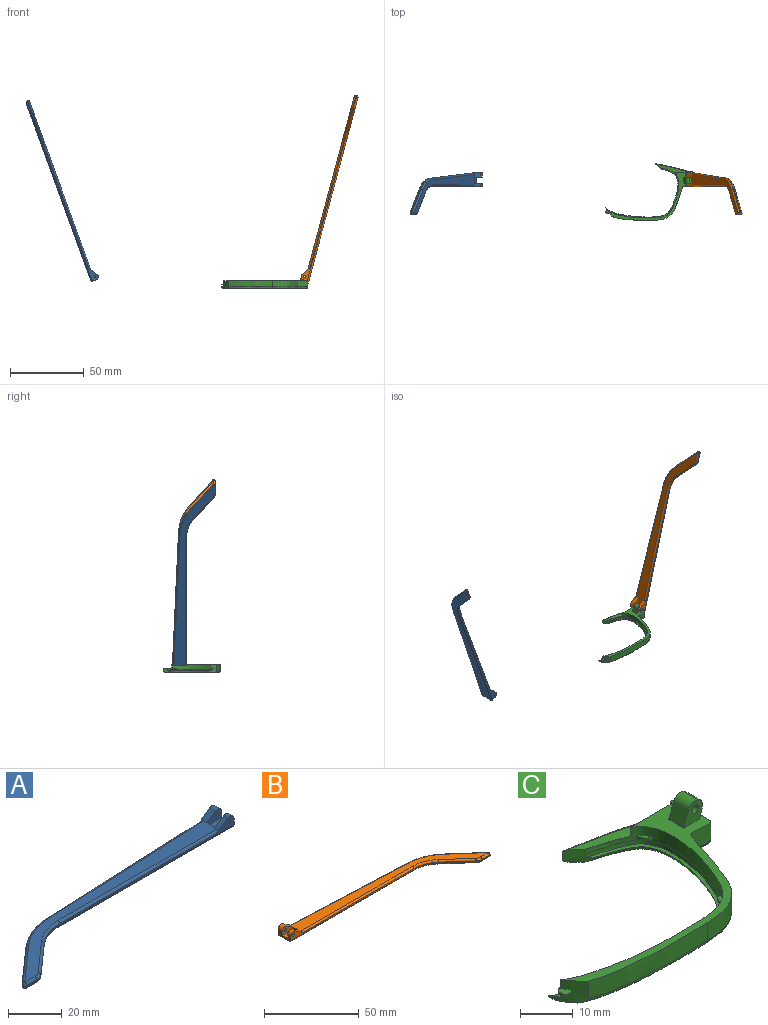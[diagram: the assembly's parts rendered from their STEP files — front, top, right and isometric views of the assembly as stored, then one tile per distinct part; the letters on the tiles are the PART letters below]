
ASSEMBLY  parts=3 mates=1
PART A: 43 faces, bbox 130.2x29.5x5.9 mm
  f0: plane 9.62x3.72mm, normal (1,0,0), area 24.7mm2, adj f1,f3,f4,f5,f10,f16,f18,f28
  f1: cylinder r=2.2mm len=3.45mm, axis (0,-1,0), area 11mm2, adj f0,f2,f4,f37
  f2: plane 6.01x3.91mm, normal (-0.55,0,0.84), area 12.7mm2, adj f1,f4,f9,f19,f37
  f3: plane 2.26x0.1mm, normal (0,0,1), area 0.1mm2, adj f0,f5,f18
  f4: plane 92.1x4.9mm, normal (0,-1,0), area 79.9mm2, adj f0,f1,f2,f14,f19,f36,f42
  f5: plane 93.42x4.13mm, normal (-0.04,1,0), area 64.8mm2, adj f0,f3,f11,f15,f17,f27,f28
  f6: plane 17.82x15.72mm, normal (-0.66,0.75,0), area 14.3mm2, adj f11,f12,f25,f30
  f7: plane 5.46x0.6mm, normal (0,-1,0), area 3.3mm2, adj f12,f13,f23,f32
  f8: plane 14.99x13.23mm, normal (0.66,-0.75,0), area 12mm2, adj f13,f14,f21,f34
  f9: plane 121.18x26.73mm, normal (0,0,1), area 627.7mm2, adj f2,f17,f19,f20,f21,f22,f23,f25
  f10: plane 129.1x27.08mm, normal (0,0,-1), area 686.5mm2, adj f0,f28,f29,f30,f32,f33,f34,f35
  f11: cylinder r=30mm len=18.52mm, axis (0,0,-1), area 12.2mm2, adj f5,f6,f26,f29
  f12: cylinder r=1mm len=1.75mm, axis (0,0,-1), area 1.5mm2, adj f6,f7,f24,f31
  f13: cylinder r=5mm len=3.31mm, axis (0,0,-1), area 2.2mm2, adj f7,f8,f22,f33
  f14: cylinder r=20mm len=13.23mm, axis (0,0,1), area 8.7mm2, adj f4,f8,f20,f35
  f15: plane 5.66x0.25mm, normal (0,0,-1), area 0.7mm2, adj f5,f17,f18
  f16: cylinder r=2.2mm len=3.45mm, axis (0,-1,0), area 14.8mm2, adj f0,f17,f18,f38
  f17: plane 6.01x3.91mm, normal (-0.55,0,0.84), area 16.9mm2, adj f5,f9,f15,f16,f18,f27,f38
  f18: plane 7.92x3.3mm, normal (0,1,0), area 15.9mm2, adj f0,f3,f15,f16,f17,f41
  f19: cylinder r=1mm len=84.18mm, axis (-1,0,0), area 131.4mm2, adj f2,f4,f9,f20
  f20: torus R=21mm, axis (0,0,1), area 23.1mm2, adj f9,f14,f19,f21
  f21: cylinder r=1mm len=15.65mm, axis (-0.75,-0.66,0), area 31.4mm2, adj f8,f9,f20,f22
  f22: torus R=4mm, axis (0,0,1), area 5.3mm2, adj f9,f13,f21,f23
  f23: cylinder r=1mm len=5.46mm, axis (-1,0,0), area 8.6mm2, adj f7,f9,f22,f24
  f24: sphere r=1mm, area 2.4mm2, adj f12,f23,f25
  f25: cylinder r=1mm len=18.48mm, axis (0.75,0.66,0), area 37.3mm2, adj f6,f9,f24,f26
  f26: torus R=29mm, axis (0,0,1), area 31.6mm2, adj f9,f11,f25,f27
  f27: cylinder r=1mm len=85.5mm, axis (1,0.04,0), area 133.5mm2, adj f5,f9,f17,f26
  f28: cylinder r=1mm len=93.46mm, axis (-1,-0.04,0), area 146.9mm2, adj f0,f5,f10,f29
  f29: torus R=29mm, axis (0,0,1), area 31.6mm2, adj f10,f11,f28,f30
  f30: cylinder r=1mm len=18.48mm, axis (-0.75,-0.66,0), area 37.3mm2, adj f6,f10,f29,f31
  f31: sphere r=1mm, area 2.4mm2, adj f12,f30,f32
  f32: cylinder r=1mm len=5.46mm, axis (1,0,0), area 8.6mm2, adj f7,f10,f31,f33
  f33: torus R=4mm, axis (0,0,1), area 5.3mm2, adj f10,f13,f32,f34
  f34: cylinder r=1mm len=15.65mm, axis (0.75,0.66,0), area 31.4mm2, adj f8,f10,f33,f35
  f35: torus R=21mm, axis (0,0,1), area 23.1mm2, adj f10,f14,f34,f36
  f36: cylinder r=1mm len=92.1mm, axis (1,0,0), area 144.7mm2, adj f0,f4,f10,f35
  f37: plane 7.92x4.7mm, normal (0,1,0), area 27mm2, adj f0,f1,f2,f39,f40,f42
  f38: plane 7.92x4.7mm, normal (0,-1,0), area 27mm2, adj f0,f16,f17,f39,f40,f41
  f39: plane 7.92x4.1mm, normal (0,0,1), area 32.5mm2, adj f0,f37,f38,f40
  f40: plane 4.1x1.4mm, normal (1,0,0), area 5.7mm2, adj f9,f37,f38,f39
  f41: cylinder r=0.5mm len=3.1mm, axis (0,-1,0), area 9.7mm2, adj f18,f38
  f42: cylinder r=0.5mm len=2.3mm, axis (0,-1,0), area 7.2mm2, adj f4,f37
PART B: 43 faces, bbox 130.2x29.5x5.9 mm
  f0: plane 9.62x3.72mm, normal (-1,0,0), area 24.7mm2, adj f1,f3,f4,f5,f10,f16,f18,f28
  f1: cylinder r=2.2mm len=3.45mm, axis (0,-1,0), area 11mm2, adj f0,f2,f4,f37
  f2: plane 6.01x3.91mm, normal (0.55,0,0.84), area 12.7mm2, adj f1,f4,f9,f19,f37
  f3: plane 2.26x0.1mm, normal (0,0,1), area 0.1mm2, adj f0,f5,f18
  f4: plane 92.1x4.9mm, normal (0,-1,0), area 78.2mm2, adj f0,f1,f2,f14,f19,f36,f42
  f5: plane 93.42x4.13mm, normal (0.04,1,0), area 64.8mm2, adj f0,f3,f11,f15,f17,f27,f28
  f6: plane 17.82x15.72mm, normal (0.66,0.75,0), area 14.3mm2, adj f11,f12,f25,f30
  f7: plane 5.46x0.6mm, normal (0,-1,0), area 3.3mm2, adj f12,f13,f23,f32
  f8: plane 14.99x13.23mm, normal (-0.66,-0.75,0), area 12mm2, adj f13,f14,f21,f34
  f9: plane 121.18x26.73mm, normal (0,0,1), area 627.7mm2, adj f2,f17,f19,f20,f21,f22,f23,f25
  f10: plane 129.1x27.08mm, normal (0,0,-1), area 686.5mm2, adj f0,f28,f29,f30,f32,f33,f34,f35
  f11: cylinder r=30mm len=18.52mm, axis (0,0,-1), area 12.2mm2, adj f5,f6,f26,f29
  f12: cylinder r=1mm len=1.75mm, axis (0,0,-1), area 1.5mm2, adj f6,f7,f24,f31
  f13: cylinder r=5mm len=3.31mm, axis (0,0,-1), area 2.2mm2, adj f7,f8,f22,f33
  f14: cylinder r=20mm len=13.23mm, axis (0,0,1), area 8.7mm2, adj f4,f8,f20,f35
  f15: plane 5.66x0.25mm, normal (0,0,-1), area 0.7mm2, adj f5,f17,f18
  f16: cylinder r=2.2mm len=3.45mm, axis (0,-1,0), area 14.8mm2, adj f0,f17,f18,f38
  f17: plane 6.01x3.91mm, normal (0.55,0,0.84), area 16.9mm2, adj f5,f9,f15,f16,f18,f27,f38
  f18: plane 7.92x3.3mm, normal (0,1,0), area 14.3mm2, adj f0,f3,f15,f16,f17,f41
  f19: cylinder r=1mm len=84.18mm, axis (1,0,0), area 131.4mm2, adj f2,f4,f9,f20
  f20: torus R=21mm, axis (0,0,1), area 23.1mm2, adj f9,f14,f19,f21
  f21: cylinder r=1mm len=15.65mm, axis (0.75,-0.66,0), area 31.4mm2, adj f8,f9,f20,f22
  f22: torus R=4mm, axis (0,0,1), area 5.3mm2, adj f9,f13,f21,f23
  f23: cylinder r=1mm len=5.46mm, axis (1,0,0), area 8.6mm2, adj f7,f9,f22,f24
  f24: sphere r=1mm, area 2.4mm2, adj f12,f23,f25
  f25: cylinder r=1mm len=18.48mm, axis (-0.75,0.66,0), area 37.3mm2, adj f6,f9,f24,f26
  f26: torus R=29mm, axis (0,0,1), area 31.6mm2, adj f9,f11,f25,f27
  f27: cylinder r=1mm len=85.5mm, axis (-1,0.04,0), area 133.5mm2, adj f5,f9,f17,f26
  f28: cylinder r=1mm len=93.46mm, axis (1,-0.04,0), area 146.9mm2, adj f0,f5,f10,f29
  f29: torus R=29mm, axis (0,0,1), area 31.6mm2, adj f10,f11,f28,f30
  f30: cylinder r=1mm len=18.48mm, axis (0.75,-0.66,0), area 37.3mm2, adj f6,f10,f29,f31
  f31: sphere r=1mm, area 2.4mm2, adj f12,f30,f32
  f32: cylinder r=1mm len=5.46mm, axis (-1,0,0), area 8.6mm2, adj f7,f10,f31,f33
  f33: torus R=4mm, axis (0,0,1), area 5.3mm2, adj f10,f13,f32,f34
  f34: cylinder r=1mm len=15.65mm, axis (-0.75,0.66,0), area 31.4mm2, adj f8,f10,f33,f35
  f35: torus R=21mm, axis (0,0,1), area 23.1mm2, adj f10,f14,f34,f36
  f36: cylinder r=1mm len=92.1mm, axis (-1,0,0), area 144.7mm2, adj f0,f4,f10,f35
  f37: plane 7.92x4.7mm, normal (0,1,0), area 25.4mm2, adj f0,f1,f2,f39,f40,f42
  f38: plane 7.92x4.7mm, normal (0,-1,0), area 25.4mm2, adj f0,f16,f17,f39,f40,f41
  f39: plane 7.92x4.1mm, normal (0,0,1), area 32.5mm2, adj f0,f37,f38,f40
  f40: plane 4.1x1.4mm, normal (-1,0,0), area 5.7mm2, adj f9,f37,f38,f39
  f41: cylinder r=0.88mm len=3.1mm, axis (0,-1,0), area 17mm2, adj f18,f38
  f42: cylinder r=0.88mm len=2.3mm, axis (0,-1,0), area 12.6mm2, adj f4,f37
PART C: 47 faces, bbox 79.8x39.4x10 mm
  f0: plane 0.12x0.12mm, normal (0,0,1), area 0mm2, adj f32,f43
  f1: plane 2.1x0.76mm, normal (-1,0,0), area 0.8mm2, adj f20,f21,f32
  f2: plane 2.1x0.76mm, normal (-0.09,-1,0), area 0.8mm2, adj f5,f21,f32
  f3: cylinder r=23.23mm len=6.29mm, axis (0,0,-1), area 27.9mm2, adj f7,f8,f9,f10,f11,f13,f14,f21
  f4: plane 23.23x5.52mm, normal (0,0,1), area 40.2mm2, adj f6,f11,f20,f46
  f5: extruded ~38.42x24.93mm, area 229.1mm2, adj f2,f6,f7,f15,f16,f17,f18,f19
  f6: cylinder r=23.23mm len=4.5mm, axis (0,0,-1), area 12.6mm2, adj f4,f5,f8,f9,f10,f11,f12,f17
  f7: extruded ~29.64x4.1mm, area 122.5mm2, adj f3,f5,f14,f21
  f8: plane 56.12x36.23mm, normal (0,0,-1), area 129.5mm2, adj f3,f6,f12,f13,f14,f15,f17,f18
  f9: extruded ~48.57x34.22mm, area 82.5mm2, adj f3,f6,f10,f11
  f10: plane 49.88x34.41mm, normal (0,0,1), area 66.1mm2, adj f3,f6,f9,f12,f13
  f11: extruded ~48.57x34.22mm, area 233.1mm2, adj f3,f4,f6,f9,f20,f21,f33,f34
  f12: bspline ~38.03x21.63mm, area 70.1mm2, adj f6,f8,f10,f13
  f13: bspline ~44.25x7.79mm, area 59.6mm2, adj f3,f8,f10,f12
  f14: bspline ~61.97x12.04mm, area 48.2mm2, adj f3,f7,f8,f15
  f15: bspline ~37.06x24.83mm, area 58.2mm2, adj f5,f8,f14,f16
  f16: bspline ~1x1mm, area 0.8mm2, adj f5,f15,f18
  f17: bspline ~25.84x6.92mm, area 37.7mm2, adj f5,f6,f8,f19
  f18: bspline ~8.96x1.23mm, area 12.6mm2, adj f5,f8,f16,f19
  f19: bspline ~1.04x1mm, area 0.7mm2, adj f5,f17,f18
  f20: plane 11.42x2.1mm, normal (0,1,0), area 24mm2, adj f1,f4,f11,f21,f45
  f21: plane 58.2x33.47mm, normal (0,0,1), area 185mm2, adj f1,f2,f3,f5,f7,f11,f20,f22
  f22: plane 0.73x0.26mm, normal (0,-1,0), area 0.1mm2, adj f21,f23,f25,f26
  f23: plane 4x0.26mm, normal (-1,0,0), area 1.1mm2, adj f21,f22,f24,f25
  f24: plane 5.07x4.86mm, normal (0,1,0), area 15.8mm2, adj f21,f23,f25,f27,f28,f29,f30,f31
  f25: plane 4x0.05mm, normal (0.34,0,0.94), area 0.2mm2, adj f22,f23,f24,f27
  f26: plane 5.02x4.86mm, normal (0,-1,0), area 15.7mm2, adj f21,f22,f27,f28,f29,f30,f31
  f27: plane 4x3.31mm, normal (-0.94,0,0.34), area 14.1mm2, adj f24,f25,f26,f30
  f28: plane 4x2.21mm, normal (0.94,0,-0.34), area 9.4mm2, adj f21,f24,f26,f29
  f29: cylinder r=1.98mm len=4mm, axis (0,-1,0), area 12.4mm2, adj f24,f26,f28,f30
  f30: cylinder r=1.98mm len=4mm, axis (0,1,0), area 12.4mm2, adj f24,f26,f27,f29
  f31: cylinder r=0.88mm len=4mm, axis (0,-1,0), area 22mm2, adj f24,f26
  f32: cone r=1mm half-angle=20deg, axis (0,0,1), area 5.1mm2, adj f0,f1,f2,f21,f42,f44
  f33: plane 2.5x1.83mm, normal (0,0,-1), area 1.7mm2, adj f11,f35
  f34: plane 2.5x1.83mm, normal (0,0,1), area 1.7mm2, adj f11,f35
  f35: cylinder r=2.28mm len=2.47mm, axis (0,0,1), area 1.7mm2, adj f11,f33,f34
  f36: cylinder r=1.3mm len=2.6mm, axis (0,0,1), area 3.7mm2, adj f3,f11,f37,f38
  f37: plane 2.61x2.6mm, normal (0,0,-1), area 4.5mm2, adj f3,f11,f36
  f38: plane 2.61x2.6mm, normal (0,0,1), area 4.5mm2, adj f3,f11,f36
  f39: plane 1.95x1.68mm, normal (0,0,-1), area 1.5mm2, adj f11,f41
  f40: plane 1.95x1.68mm, normal (0,0,1), area 1.5mm2, adj f11,f41
  f41: cylinder r=1.3mm len=1.93mm, axis (0,0,1), area 1.5mm2, adj f11,f39,f40
  f42: bspline ~0.75x0.3mm, area 0.1mm2, adj f5,f32,f43
  f43: bspline ~0.5x0.44mm, area 0.2mm2, adj f0,f5,f42,f44
  f44: bspline ~1.05x0.58mm, area 0.3mm2, adj f5,f32,f43,f45
  f45: bspline ~0.42x0.33mm, area 0mm2, adj f5,f20,f44,f46
  f46: bspline ~25.09x6.11mm, area 11.4mm2, adj f4,f5,f6,f45
PLACE A rot(axis=(0,1,0),70deg) t=(-84.77,-5.75,56)mm
PLACE B rot(axis=(0,-1,0),75deg) t=(68.2,-5.75,-61.61)mm
PLACE C t=(10.15,-1.13,-5.77)mm
MATE revolute B.f41 <-> C.f29  axis (0,-1,0) through (81.2,2.72,1.21)mm
